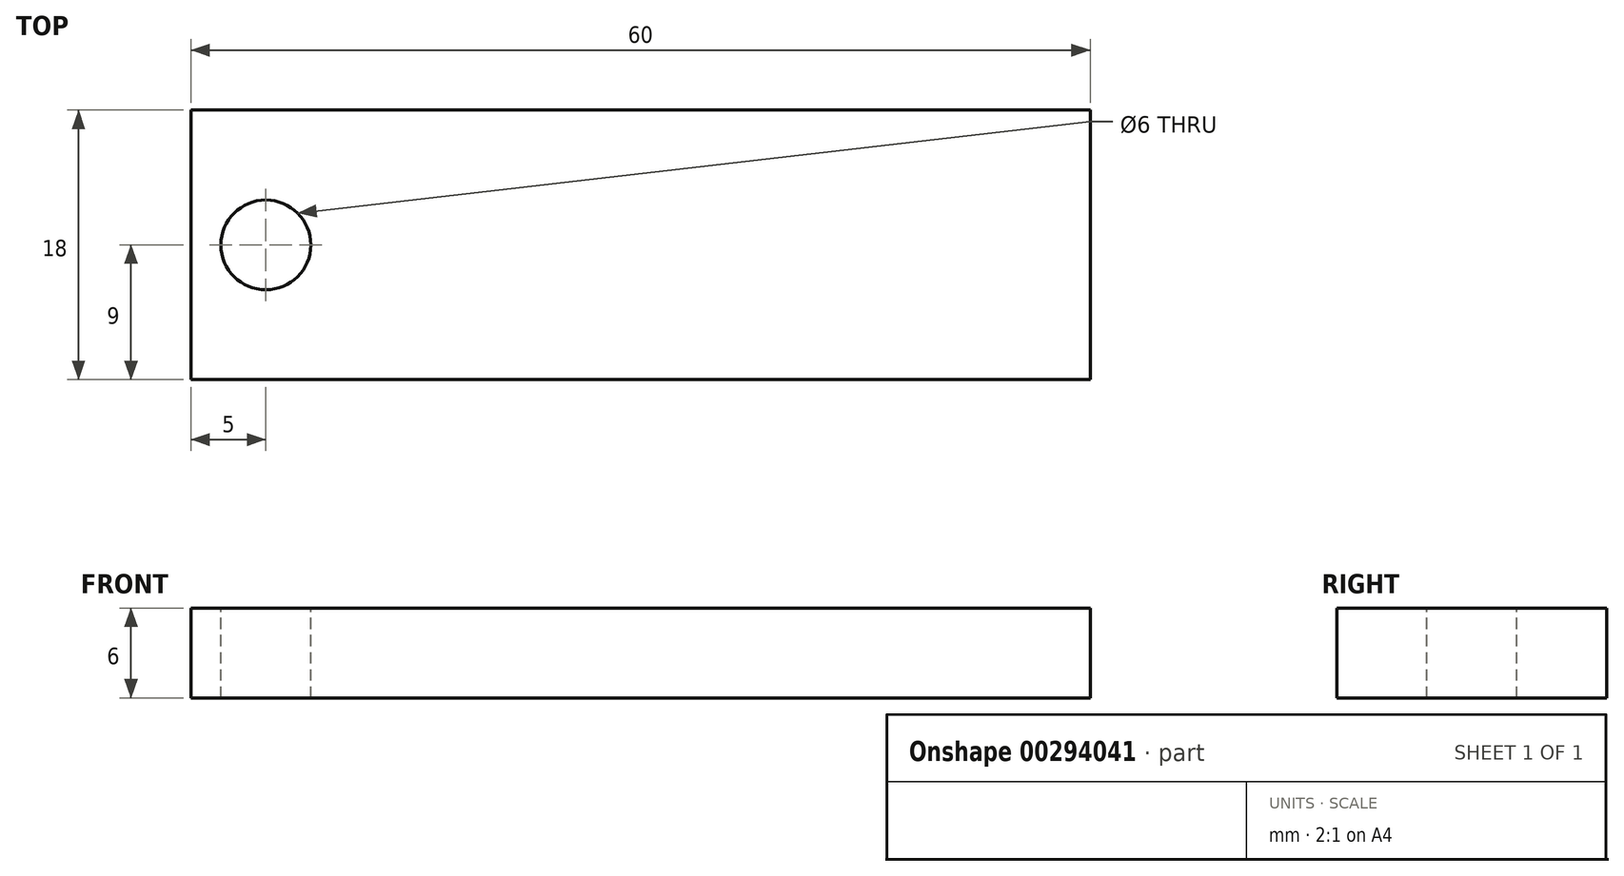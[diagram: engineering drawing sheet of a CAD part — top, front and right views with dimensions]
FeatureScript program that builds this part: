
annotation { "Feature Type Name" : "Feature", "Feature Type Description" : "" }
export const myFeature = defineFeature(function(context is Context, id is Id, definition is map)
    precondition{}
    {
        {
            var Q0;
            Q0=qCreatedBy(makeId("Top.planeOp"),FACE);
            var sketch = newSketch(context, id + "F0", { "sketchPlane" : qUnion([Q0])});
            skLineSegment(sketch, "E0.bottom", {"start": v(-30, 9) * mm, "end": v(30, 9) * mm});
            skLineSegment(sketch, "E0.top", {"start": v(-30, -9) * mm, "end": v(30, -9) * mm});
            skLineSegment(sketch, "E0.left", {"start": v(-30, 9) * mm, "end": v(-30, -9) * mm});
            skLineSegment(sketch, "E0.right", {"start": v(30, 9) * mm, "end": v(30, -9) * mm});
            skPoint(sketch, "E0.middle", {"position": v(0, 0) * mm});
            skSolve(sketch);
        }
        {
            var Q0;
            Q0 = qSketchRegion(id + "F0", true);
            extrude(context, id + "F1", {"entities" : qUnion([Q0]), "depth" : 6 * mm, "offsetDistance" : 25 * mm});
        }
        {
            var Q0;
            Q0=makeQuery(id+"F1.opExtrude","CAP_FACE",FACE,{"disambiguationData":[OSD([sQuery(id+"F0.wireOp",EDGE,"E0.bottom"),sQuery(id+"F0.wireOp",EDGE,"E0.top"),sQuery(id+"F0.wireOp",EDGE,"E0.left"),sQuery(id+"F0.wireOp",EDGE,"E0.right")])],"isStart":false});
            var sketch = newSketch(context, id + "F2", { "sketchPlane" : qUnion([Q0])});
            skCircle(sketch, "E1", {"center": v(-25, 0) * mm, "radius": 3 * mm});
            skLineSegment(sketch, "E2", {"start": v(-30, 0) * mm, "end": v(30, 0) * mm, "construction": true});
            skSolve(sketch);
        }
        {
            var Q0;
            Q0 = qSketchRegion(id + "F2", true);
            extrude(context, id + "F3", {"entities" : qUnion([Q0]), "operationType" : NewBodyOperationType.REMOVE, "endBound" : BoundingType.UP_TO_NEXT, "oppositeDirection" : true, "depth" : 25 * mm, "offsetDistance" : 25 * mm});
        }
    });
